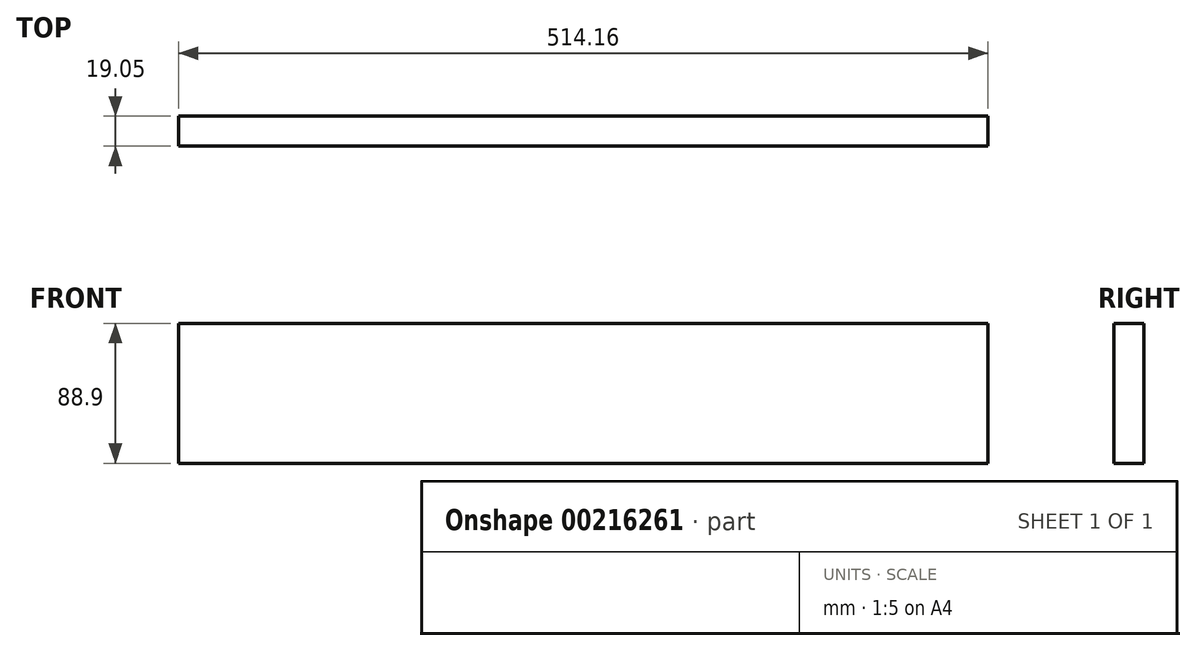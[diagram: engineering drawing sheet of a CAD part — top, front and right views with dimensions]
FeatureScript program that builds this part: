
annotation { "Feature Type Name" : "Feature", "Feature Type Description" : "" }
export const myFeature = defineFeature(function(context is Context, id is Id, definition is map)
    precondition{}
    {
        {
            var Q0;
            Q0=qCreatedBy(makeId("Front.planeOp"),FACE);
            var sketch = newSketch(context, id + "F0", { "sketchPlane" : qUnion([Q0])});
            skLineSegment(sketch, "E0", {"start": v(-2116.43, -2226.84) * mm, "end": v(-1602.27, -2226.84) * mm});
            skLineSegment(sketch, "E1", {"start": v(-1602.27, -2226.84) * mm, "end": v(-1602.27, -2315.74) * mm});
            skLineSegment(sketch, "E2", {"start": v(-1602.27, -2315.74) * mm, "end": v(-2116.43, -2315.74) * mm});
            skLineSegment(sketch, "E3", {"start": v(-2116.43, -2315.74) * mm, "end": v(-2116.43, -2226.84) * mm});
            skSolve(sketch);
        }
        {
            var Q0;
            Q0=makeQuery(id+"F0.imprint","IMPRINT",FACE,{"disambiguationData":[TD([[makeQuery(id+"F0.imprint","IMPRINT",EDGE,{"derivedFrom":sQuery(id+"F0.wireOp",EDGE,"E0")}),-1.0]])]});
            extrude(context, id + "F1", {"entities" : qUnion([Q0]), "depth" : 19.05 * mm});
        }
    });
